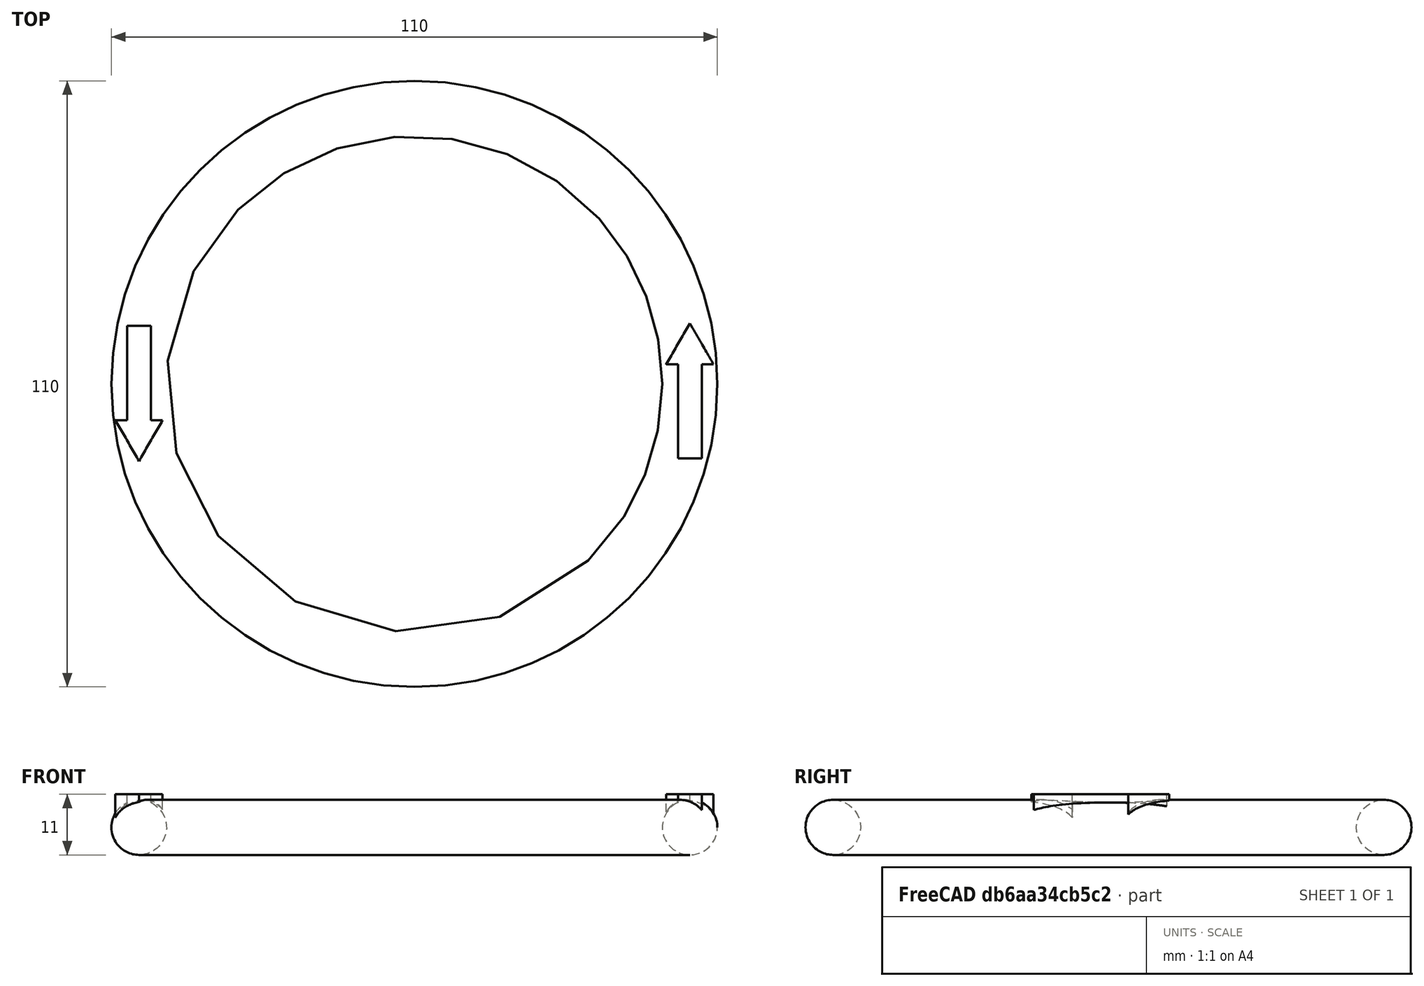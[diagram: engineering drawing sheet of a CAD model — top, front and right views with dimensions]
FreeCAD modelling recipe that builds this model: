
FCSTD DOCUMENT  (FreeCAD 0.15R4671 (Git))
Label: current_loop
License: All rights reserved
LicenseURL: http://en.wikipedia.org/wiki/All_rights_reserved
objects: Part::Feature×3, Part::Part2DObjectPython×2, Part::Extrusion×2, Part::Torus×1, Part::MultiFuse×1, Mesh::Feature×1
note: 9 computed .brp shape members not serialized (recipe doc carries the construction recipe); baked Part::Feature solids carry a one-line shape summary decoded from their .brp

FEATURE [Part::Torus] Torus
  Angle1 = 180
  Angle2 = -180
  Angle3 = 360
  Radius1 = 50
  Radius2 = 5
FEATURE [Part::Feature] Face
  shape: bbox 8.605 x 34.58 x 2e-07 mm, 1 faces, 0 solids (baked)
FEATURE [Part::Feature] Face001
  shape: bbox 17.16 x 14.86 x 2e-07 mm, 1 faces, 0 solids (baked)
FEATURE [Part::Part2DObjectPython] Fusion  # Draft 2D object (typed FeaturePython)
  Base = -> Face
  ChamferSize = 0
  Closed = false
  End = (21.7456,-19.5466,0)
  FilletRadius = 0
  Length = 0
  MakeFace = true
  Points = (7) [(26.0236,-19.5466,0),(17.4435,-4.68592,0),(8.86199,-19.5466,0),(13.1405,-19.5466,0),(13.1405,-53.7696,0),(21.7456,-53.7696,0),(21.7456,-19.5466,0)]
  Start = (26.0236,-19.5466,0)
  Tool = -> Face001
FEATURE [Part::Part2DObjectPython] Clone2D  label="Clone of Fusion (2D)"  # Draft 2D object (typed FeaturePython)
  Objects = -> [Fusion]
  Placement = pos=(41.2783,13.343,0) rot=(0,0,1;0rad)
  Scale = (0.5,0.5,0.55)
FEATURE [Part::Feature] Clone2D001  label="Clone of Fusion (2D)001"
  Placement = pos=(-41.2783,-16.343,0) rot=(0,0,1;3.14159rad)
  shape: bbox 8.581 x 24.54 x 2e-07 mm, 1 faces, 0 solids (baked)
FEATURE [Part::Extrusion] Extrude
  Base = -> Clone2D
  Dir = (0,0,6)
  Solid = false
FEATURE [Part::Extrusion] Extrude002
  Base = -> Clone2D001
  Dir = (0,0,6)
  Solid = false
FEATURE [Part::MultiFuse] Fusion001
  Shapes = -> [Torus,Extrude,Extrude002]
FEATURE [Mesh::Feature] Mesh  label="Fusion001 (Meshed)"
